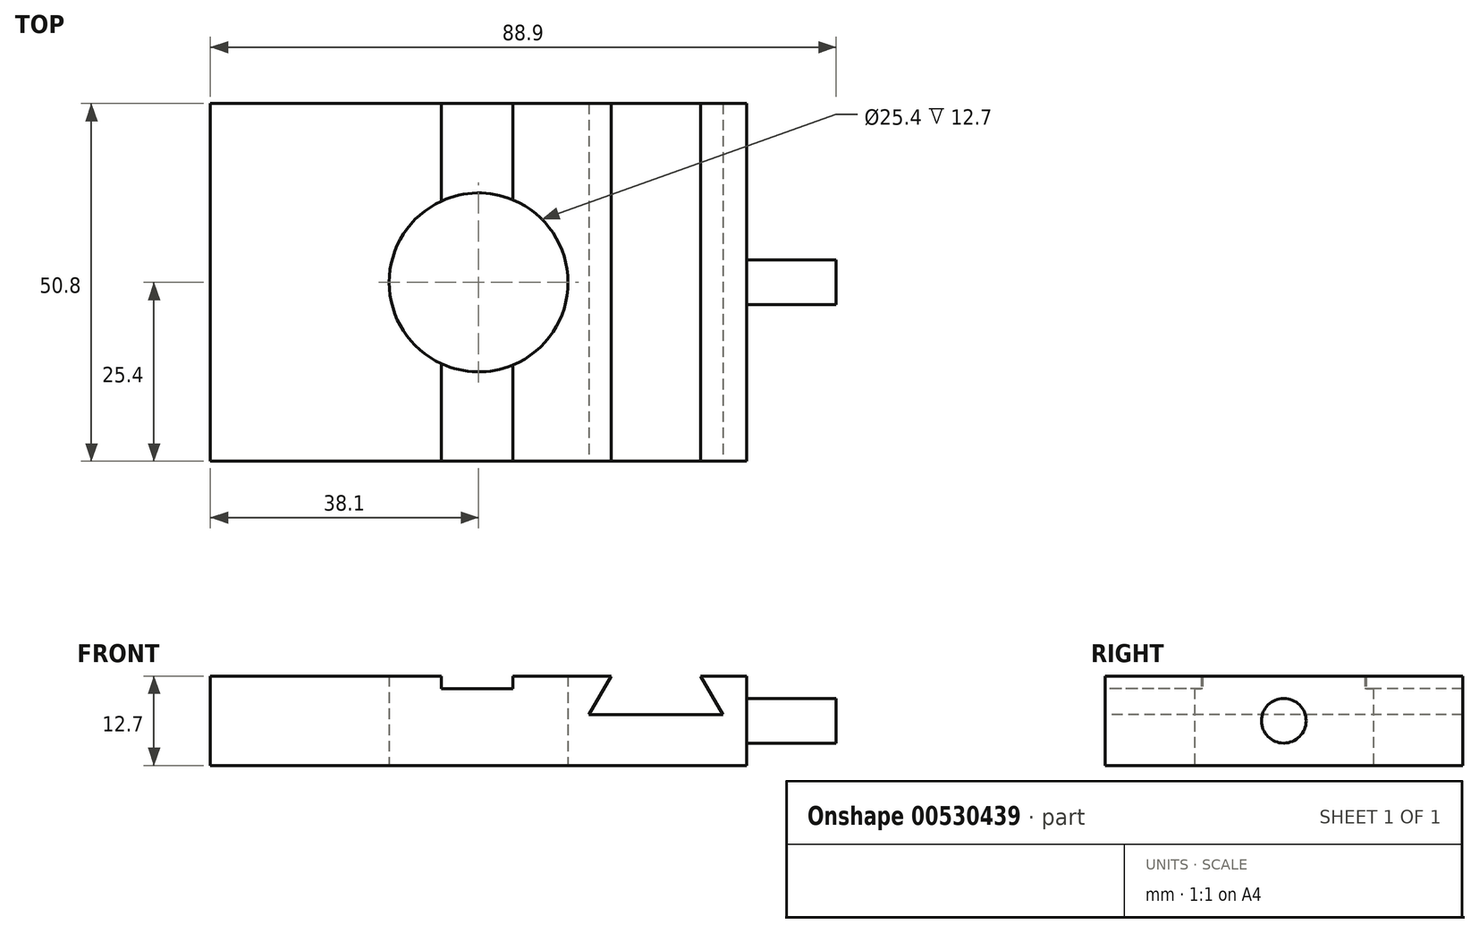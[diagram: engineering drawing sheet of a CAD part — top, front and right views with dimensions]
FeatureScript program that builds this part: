
annotation { "Feature Type Name" : "Feature", "Feature Type Description" : "" }
export const myFeature = defineFeature(function(context is Context, id is Id, definition is map)
    precondition{}
    {
        {
            var Q0;
            Q0=qCreatedBy(makeId("Top.planeOp"),FACE);
            var sketch = newSketch(context, id + "F0", { "sketchPlane" : qUnion([Q0])});
            skLineSegment(sketch, "E0.bottom", {"start": v(38.1, -25.4) * mm, "end": v(-38.1, -25.4) * mm});
            skLineSegment(sketch, "E0.top", {"start": v(38.1, 25.4) * mm, "end": v(-38.1, 25.4) * mm});
            skLineSegment(sketch, "E0.left", {"start": v(38.1, -25.4) * mm, "end": v(38.1, 25.4) * mm});
            skLineSegment(sketch, "E0.right", {"start": v(-38.1, -25.4) * mm, "end": v(-38.1, 25.4) * mm});
            skPoint(sketch, "E0.middle", {"position": v(0, 0) * mm});
            skCircle(sketch, "E1", {"center": v(0, 0) * mm, "radius": 12.7 * mm});
            skSolve(sketch);
        }
        {
            var Q0;
            Q0 = qSketchRegion(id + "F0", true);
            extrude(context, id + "F1", {"entities" : qUnion([Q0]), "depth" : 12.7 * mm, "offsetDistance" : 25.4 * mm});
        }
        {
            var Q0;
            Q0=makeQuery(id+"F1.opExtrude","CAP_FACE",FACE,{"disambiguationData":[OSD([sQuery(id+"F0.wireOp",EDGE,"E0.bottom"),sQuery(id+"F0.wireOp",EDGE,"E0.top"),sQuery(id+"F0.wireOp",EDGE,"E0.left"),sQuery(id+"F0.wireOp",EDGE,"E0.right"),sQuery(id+"F0.wireOp",EDGE,"E1")])],"isStart":false});
            var sketch = newSketch(context, id + "F2", { "sketchPlane" : qUnion([Q0])});
            skLineSegment(sketch, "E2.bottom", {"start": v(-29.64, -25.4) * mm, "end": v(-23.3, -25.4) * mm});
            skLineSegment(sketch, "E2.top", {"start": v(-29.64, 25.4) * mm, "end": v(-23.3, 25.4) * mm});
            skLineSegment(sketch, "E2.left", {"start": v(-29.64, -25.4) * mm, "end": v(-29.64, 25.4) * mm});
            skLineSegment(sketch, "E2.right", {"start": v(-23.3, -25.4) * mm, "end": v(-23.3, 25.4) * mm});
            skLineSegment(sketch, "E3.bottom", {"start": v(-5.3, 25.4) * mm, "end": v(4.87, 25.4) * mm});
            skLineSegment(sketch, "E3.top", {"start": v(-5.3, -25.4) * mm, "end": v(4.87, -25.4) * mm});
            skLineSegment(sketch, "E3.left", {"start": v(-5.3, 25.4) * mm, "end": v(-5.3, -25.4) * mm});
            skLineSegment(sketch, "E3.right", {"start": v(4.87, 25.4) * mm, "end": v(4.87, -25.4) * mm});
            skSolve(sketch);
        }
        {
            var Q0;
            {var subQ0=sQuery(id+"F2.wireOp",EDGE,"E3.bottom");Q0=makeQuery(id+"F2.imprint","IMPRINT",FACE,{"disambiguationData":[TD([[makeQuery(id+"F2.imprint","IMPRINT",EDGE,{"derivedFrom":subQ0}),1.0]])]});}
            var Q1;
            {var subQ0=sQuery(id+"F2.wireOp",EDGE,"E3.top");Q1=makeQuery(id+"F2.imprint","IMPRINT",FACE,{"disambiguationData":[TD([[makeQuery(id+"F2.imprint","IMPRINT",EDGE,{"derivedFrom":subQ0}),-1.0]])]});}
            var Q2;
            {var subQ0=sQuery(id+"F2.wireOp",EDGE,"E3.left");var subQ1=makeQuery(id+"F1.opExtrude","CAP_EDGE",EDGE,{"disambiguationData":[OSD([sQuery(id+"F0.wireOp",EDGE,"E1")])],"isStart":false});var subQ2=makeQuery(id+"F2.imprint","INTERSECT",VERTEX,{"disambiguationData":[OD(0.0)],"derivedFrom":[subQ1,subQ0]});Q2=makeQuery(id+"F2.imprint","IMPRINT",FACE,{"disambiguationData":[TD([[makeQuery(id+"F2.imprint","IMPRINT",EDGE,{"disambiguationData":[TD([[subQ2,-1.0]])],"derivedFrom":subQ0}),1.0]])]});}
            extrude(context, id + "F3", {"entities" : qUnion([Q0, Q1, Q2]), "operationType" : NewBodyOperationType.REMOVE, "oppositeDirection" : true, "depth" : 1.78 * mm, "offsetDistance" : 25.4 * mm});
        }
        {
            var Q0;
            Q0=makeQuery(id+"F1.opExtrude","SWEPT_FACE",FACE,{"disambiguationData":[OSD([sQuery(id+"F0.wireOp",EDGE,"E0.bottom")])]});
            var sketch = newSketch(context, id + "F4", { "sketchPlane" : qUnion([Q0])});
            skLineSegment(sketch, "E4", {"start": v(18.84, 12.7) * mm, "end": v(15.66, 7.2) * mm});
            skLineSegment(sketch, "E5", {"start": v(15.66, 7.2) * mm, "end": v(34.71, 7.2) * mm});
            skLineSegment(sketch, "E6", {"start": v(34.71, 7.2) * mm, "end": v(31.54, 12.7) * mm});
            skLineSegment(sketch, "E7", {"start": v(31.54, 12.7) * mm, "end": v(18.84, 12.7) * mm});
            skLineSegment(sketch, "E8", {"start": v(25.19, 7.2) * mm, "end": v(25.19, 12.7) * mm, "construction": true});
            skSolve(sketch);
        }
        {
            var Q0;
            Q0=makeQuery(id+"F4.imprint","IMPRINT",FACE,{"disambiguationData":[TD([[makeQuery(id+"F4.imprint","IMPRINT",EDGE,{"derivedFrom":sQuery(id+"F4.wireOp",EDGE,"E4")}),1.0]])]});
            extrude(context, id + "F5", {"entities" : qUnion([Q0]), "operationType" : NewBodyOperationType.REMOVE, "endBound" : BoundingType.UP_TO_NEXT, "oppositeDirection" : true, "depth" : 18.9 * mm, "offsetDistance" : 25.4 * mm});
        }
        {
            var Q0;
            Q0=makeQuery(id+"F1.opExtrude","SWEPT_FACE",FACE,{"disambiguationData":[OSD([sQuery(id+"F0.wireOp",EDGE,"E0.left")])]});
            var sketch = newSketch(context, id + "F6", { "sketchPlane" : qUnion([Q0])});
            skPoint(sketch, "E9", {"position": v(0, 12.7) * mm});
            skPoint(sketch, "E10", {"position": v(0, 0) * mm});
            skPoint(sketch, "E11", {"position": v(25.4, 6.35) * mm});
            skPoint(sketch, "E12", {"position": v(-25.4, 6.35) * mm});
            skPoint(sketch, "E13", {"position": v(0, 6.35) * mm});
            skCircle(sketch, "E14", {"center": v(0, 6.35) * mm, "radius": 3.18 * mm});
            skSolve(sketch);
        }
        {
            var Q0;
            Q0 = qSketchRegion(id + "F6", true);
            extrude(context, id + "F7", {"entities" : qUnion([Q0]), "operationType" : NewBodyOperationType.ADD, "depth" : 12.7 * mm, "offsetDistance" : 25.4 * mm});
        }
    });
